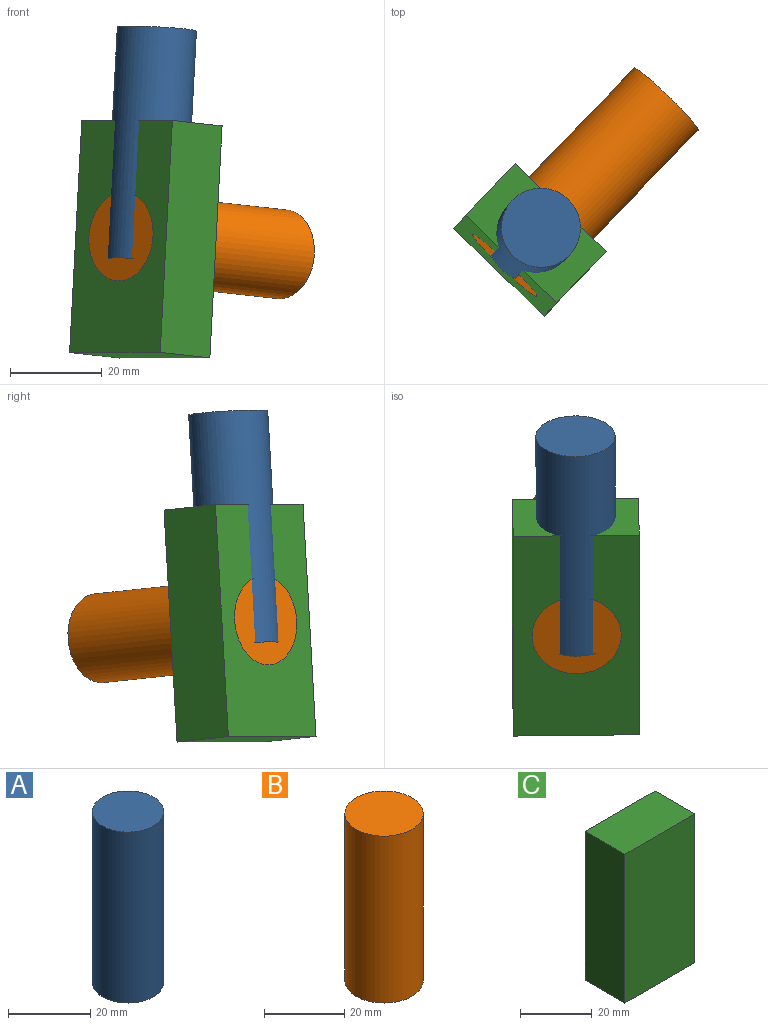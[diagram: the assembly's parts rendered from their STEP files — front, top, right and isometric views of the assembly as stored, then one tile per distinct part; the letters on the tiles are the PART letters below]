
ASSEMBLY  parts=3 mates=2
PART A: 3 faces, bbox 17.3x17.3x50.8 mm
  f0: cylinder r=8.65mm len=50.8mm, axis (0,0,-1), area 2761.1mm2, adj f1,f2
  f1: plane 17.3x17.3mm, normal (0,0,1), area 235.1mm2, adj f0
  f2: plane 17.3x17.3mm, normal (0,0,-1), area 235.1mm2, adj f0
PART B: 3 faces, bbox 19.5x19.5x50.8 mm
  f0: cylinder r=9.73mm len=50.8mm, axis (0,0,-1), area 3106.8mm2, adj f1,f2
  f1: plane 19.47x19.47mm, normal (0,0,1), area 297.6mm2, adj f0
  f2: plane 19.47x19.47mm, normal (0,0,-1), area 297.6mm2, adj f0
PART C: 6 faces, bbox 27.5x15.6x50.8 mm
  f0: plane 50.8x15.65mm, normal (-1,0,0), area 795mm2, adj f1,f3,f4,f5
  f1: plane 50.8x27.53mm, normal (0,-1,0), area 1398.4mm2, adj f0,f2,f4,f5
  f2: plane 50.8x15.65mm, normal (1,0,0), area 795mm2, adj f1,f3,f4,f5
  f3: plane 50.8x27.53mm, normal (0,1,0), area 1398.4mm2, adj f0,f2,f4,f5
  f4: plane 27.53x15.65mm, normal (0,0,1), area 430.8mm2, adj f0,f1,f2,f3
  f5: plane 27.53x15.65mm, normal (0,0,-1), area 430.8mm2, adj f0,f1,f2,f3
PLACE A rot(axis=(0.93,-0.38,-0.01),175.9deg) t=(24.42,-19,58.92)mm
PLACE B rot(axis=(0.73,0.15,-0.67),131.2deg) t=(-57.14,32.83,19.6)mm
PLACE C rot(axis=(-0.09,0.04,-0.99),44.3deg) t=(-41.67,-76.84,-6.02)mm
MATE revolute B.f0 <-> C.f1  axis (-0.69,-0.72,0.08) through (-56.85,-38.52,18.11)mm
MATE slider A.f0 <-> C.f4  axis (-0.05,-0.06,-1) through (-51.67,-33.18,12.76)mm
